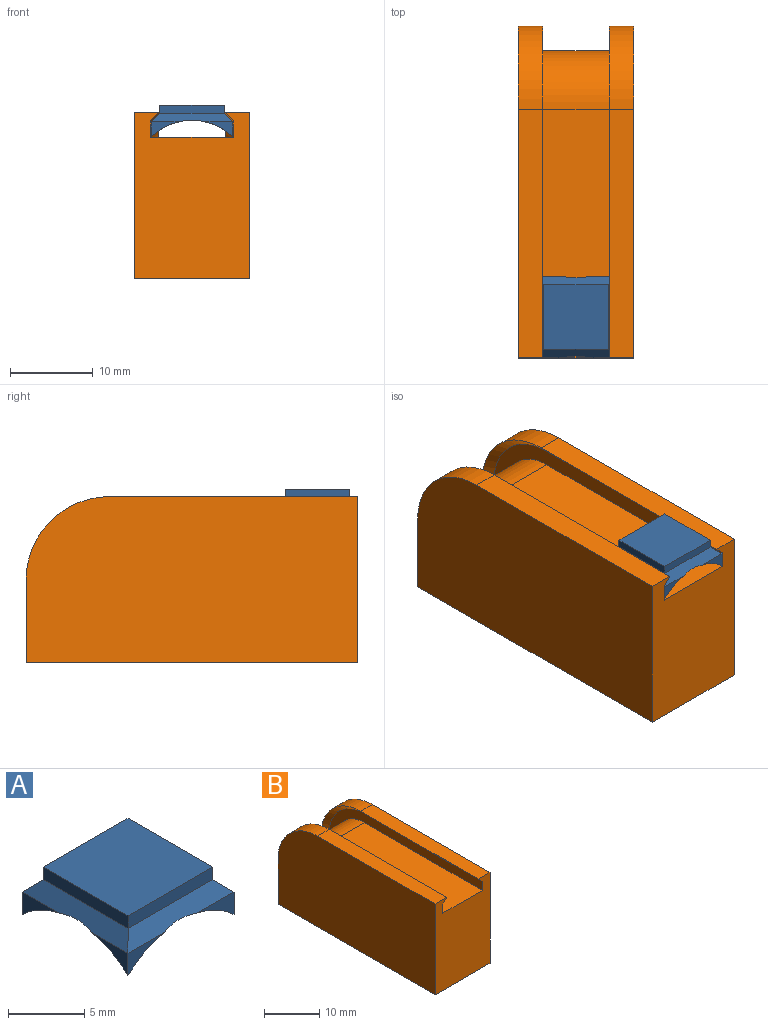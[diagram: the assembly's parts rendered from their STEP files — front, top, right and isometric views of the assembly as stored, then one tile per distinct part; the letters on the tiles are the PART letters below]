
ASSEMBLY  parts=2 mates=1
PART A: 21 faces, bbox 9.8x9.8x3.8 mm
  f0: plane 3.35x1.8mm, normal (1,0,0), area 2.4mm2, adj f5,f11,f13
  f1: plane 3.35x1.8mm, normal (-1,0,0), area 2.4mm2, adj f6,f8,f14
  f2: plane 3.35x1.8mm, normal (0,-1,0), area 2.4mm2, adj f4,f10,f12
  f3: plane 3.35x1.8mm, normal (0,1,0), area 2.4mm2, adj f7,f9,f15
  f4: cylinder r=7.07mm len=9.8mm, axis (0,-1,0), area 24.8mm2, adj f2,f5,f6,f8,f12
  f5: cylinder r=7.07mm len=9.8mm, axis (-1,0,0), area 24.8mm2, adj f0,f4,f7,f10,f13
  f6: plane 3.35x1.8mm, normal (0,-1,0), area 2.4mm2, adj f1,f4,f12
  f7: cylinder r=7.07mm len=9.8mm, axis (0,-1,0), area 24.8mm2, adj f3,f5,f8,f11,f15
  f8: cylinder r=7.07mm len=9.8mm, axis (-1,0,0), area 24.8mm2, adj f1,f4,f7,f9,f14
  f9: plane 3.35x1.8mm, normal (-1,0,0), area 2.4mm2, adj f3,f8,f14
  f10: plane 3.35x1.8mm, normal (1,0,0), area 2.4mm2, adj f2,f5,f13
  f11: plane 3.35x1.8mm, normal (0,1,0), area 2.4mm2, adj f0,f7,f15
  f12: plane 9.8x1mm, normal (0,-0.71,0.71), area 11.9mm2, adj f2,f4,f6,f13,f14,f18
  f13: plane 9.8x1mm, normal (0.71,0,0.71), area 11.9mm2, adj f0,f5,f10,f12,f15,f19
  f14: plane 9.8x1mm, normal (-0.71,0,0.71), area 11.9mm2, adj f1,f8,f9,f12,f15,f17
  f15: plane 9.8x1mm, normal (0,0.71,0.71), area 11.9mm2, adj f3,f7,f11,f13,f14,f16
  f16: plane 7.8x1mm, normal (0,1,0), area 7.8mm2, adj f15,f17,f19,f20
  f17: plane 7.8x1mm, normal (-1,0,0), area 7.8mm2, adj f14,f16,f18,f20
  f18: plane 7.8x1mm, normal (0,-1,0), area 7.8mm2, adj f12,f17,f19,f20
  f19: plane 7.8x1mm, normal (1,0,0), area 7.8mm2, adj f13,f16,f18,f20
  f20: plane 7.8x7.8mm, normal (0,0,1), area 60.8mm2, adj f16,f17,f18,f19
PART B: 21 faces, bbox 14x40.1x20.1 mm
  f0: plane 40.07x20.07mm, normal (-1,0,0), area 782.5mm2, adj f8,f9,f14,f19,f20
  f1: plane 40.07x20.07mm, normal (1,0,0), area 782.5mm2, adj f2,f9,f10,f15,f20
  f2: plane 30x3mm, normal (0,0,1), area 90mm2, adj f1,f3,f9,f10
  f3: plane 30x1mm, normal (-0.71,0,-0.71), area 42.4mm2, adj f2,f4,f9,f11
  f4: plane 39.07x19.07mm, normal (-1,0,0), area 105.4mm2, adj f3,f5,f9,f11,f12,f16,f17,f20
  f5: plane 30x10mm, normal (0,0,1), area 300mm2, adj f4,f6,f9,f12
  f6: plane 39.07x19.07mm, normal (1,0,0), area 105.4mm2, adj f5,f7,f9,f12,f13,f17,f18,f20
  f7: plane 30x1mm, normal (0.71,0,-0.71), area 42.4mm2, adj f6,f8,f9,f13
  f8: plane 30x3mm, normal (0,0,1), area 90mm2, adj f0,f7,f9,f14
  f9: plane 20.07x14mm, normal (0,-1,0), area 252mm2, adj f0,f1,f2,f3,f4,f5,f6,f7
  f10: cylinder r=10.07mm len=10.07mm, axis (1,0,0), area 47.5mm2, adj f1,f2,f11,f15
  f11: cone r=10.07mm half-angle=45deg, axis (-1,0,0), area 21.3mm2, adj f3,f4,f10,f16
  f12: cylinder r=7.07mm len=10mm, axis (1,0,0), area 111.1mm2, adj f4,f5,f6,f17
  f13: cone r=9.07mm half-angle=45deg, axis (1,0,0), area 21.3mm2, adj f6,f7,f14,f18
  f14: cylinder r=10.07mm len=10.07mm, axis (1,0,0), area 47.5mm2, adj f0,f8,f13,f19
  f15: plane 10x3mm, normal (0,1,0), area 30mm2, adj f1,f10,f16,f20
  f16: plane 10x1mm, normal (-0.71,-0.71,0), area 14.1mm2, adj f4,f11,f15,f20
  f17: plane 10x10mm, normal (0,1,0), area 100mm2, adj f4,f6,f12,f20
  f18: plane 10x1mm, normal (0.71,-0.71,0), area 14.1mm2, adj f6,f13,f19,f20
  f19: plane 10x3mm, normal (0,1,0), area 30mm2, adj f0,f14,f18,f20
  f20: plane 40.07x14mm, normal (0,0,-1), area 532mm2, adj f0,f1,f4,f6,f9,f15,f16,f17
PLACE A t=(0,4.9,9.51)mm
PLACE B t=(0,15,8.51)mm
MATE slider B.f9 <-> A.f6  axis (0,-1,0) through (-5,0,8.01)mm
